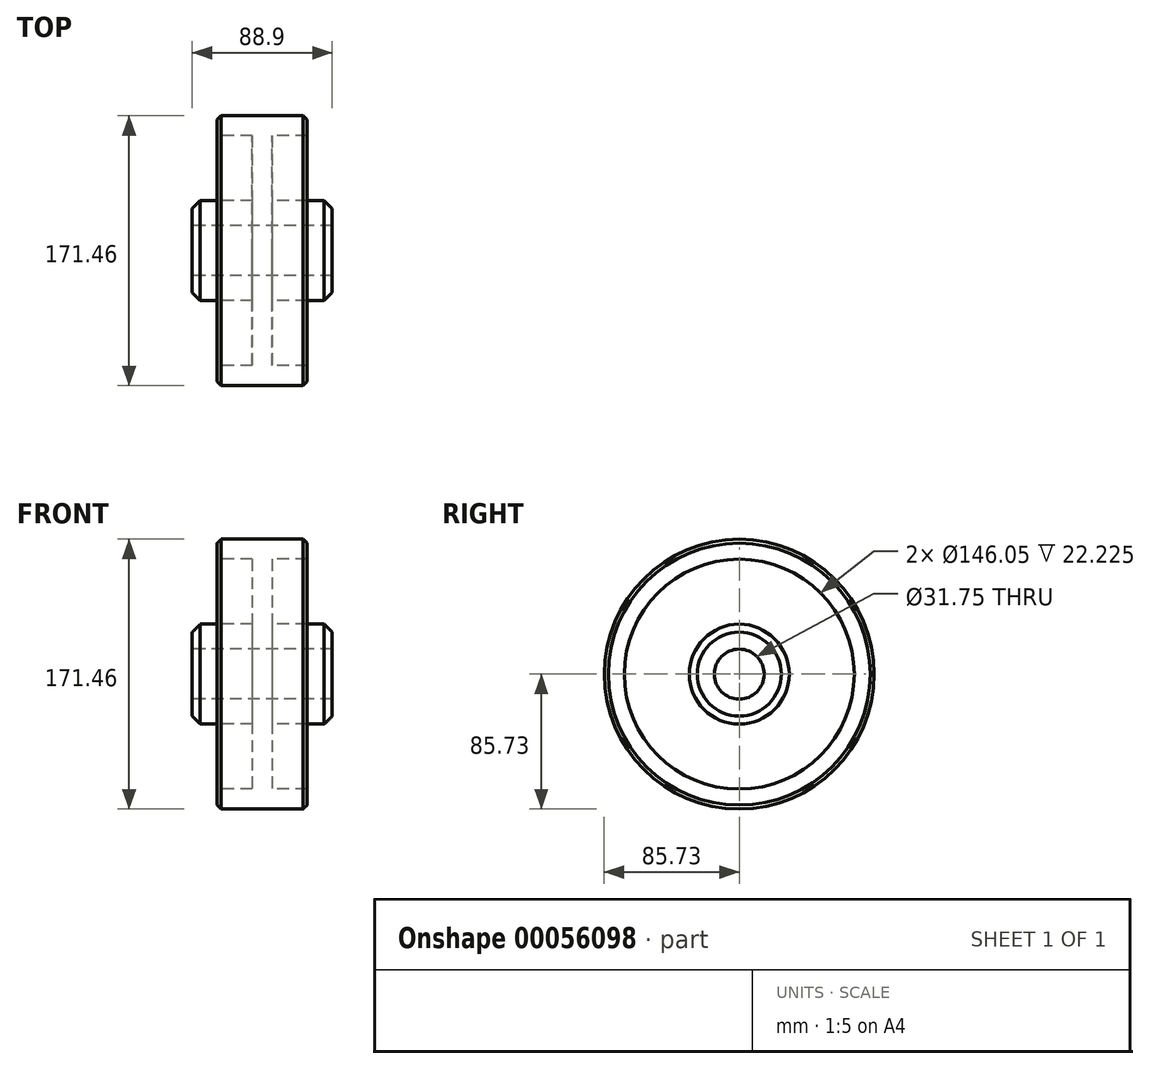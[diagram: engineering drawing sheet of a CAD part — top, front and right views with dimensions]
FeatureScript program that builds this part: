
annotation { "Feature Type Name" : "Feature", "Feature Type Description" : "" }
export const myFeature = defineFeature(function(context is Context, id is Id, definition is map)
    precondition{}
    {
        {
            var Q0;
            Q0=qCreatedBy(makeId("Front.planeOp"),FACE);
            var sketch = newSketch(context, id + "F0", { "sketchPlane" : qUnion([Q0])});
            skLineSegment(sketch, "E0", {"start": v(-28.57, 85.73) * mm, "end": v(28.57, 85.73) * mm});
            skLineSegment(sketch, "E1", {"start": v(28.57, 85.73) * mm, "end": v(28.57, 73.03) * mm});
            skLineSegment(sketch, "E2", {"start": v(28.57, 73.02) * mm, "end": v(6.35, 73.02) * mm});
            skLineSegment(sketch, "E3", {"start": v(6.35, 73.02) * mm, "end": v(6.35, 31.75) * mm});
            skLineSegment(sketch, "E4", {"start": v(6.35, 31.75) * mm, "end": v(44.45, 31.75) * mm});
            skLineSegment(sketch, "E5", {"start": v(44.45, 31.75) * mm, "end": v(44.45, 15.88) * mm});
            skLineSegment(sketch, "E6", {"start": v(44.45, 15.88) * mm, "end": v(-44.45, 15.87) * mm});
            skLineSegment(sketch, "E7", {"start": v(-44.45, 15.88) * mm, "end": v(-44.45, 31.75) * mm});
            skLineSegment(sketch, "E8", {"start": v(-44.45, 31.75) * mm, "end": v(-6.35, 31.75) * mm});
            skLineSegment(sketch, "E9", {"start": v(-6.35, 31.75) * mm, "end": v(-6.35, 73.02) * mm});
            skLineSegment(sketch, "E10", {"start": v(-6.35, 73.02) * mm, "end": v(-28.57, 73.02) * mm});
            skLineSegment(sketch, "E11", {"start": v(-28.58, 73.03) * mm, "end": v(-28.58, 85.73) * mm});
            skLineSegment(sketch, "E12", {"start": v(0, 0) * mm, "end": v(0, 277.02) * mm, "construction": true});
            skLineSegment(sketch, "E13", {"start": v(-347.66, 0) * mm, "end": v(344.49, 0) * mm, "construction": true});
            skSolve(sketch);
        }
        {
            var Q0;
            Q0 = qSketchRegion(id + "F0", true);
            var Q1;
            Q1=sQuery(id+"F0.wireOp",EDGE,"E13");
            revolve(context, id + "F1", {"entities" : qUnion([Q0]), "axis" : qUnion([Q1]), "revolveType" : RevolveType.FULL});
        }
        {
            var Q0;
            Q0=makeQuery(id+"F1.opRevolve","SWEPT_EDGE",EDGE,{"disambiguationData":[OSD([sQuery(id+"F0.wireOp",EDGE,"E0"),sQuery(id+"F0.wireOp",EDGE,"E11")])]});
            var Q1;
            Q1=makeQuery(id+"F1.opRevolve","SWEPT_EDGE",EDGE,{"disambiguationData":[OSD([sQuery(id+"F0.wireOp",EDGE,"E0"),sQuery(id+"F0.wireOp",EDGE,"E1")])]});
            chamfer(context, id + "F2", {"entities" : qUnion([Q0, Q1]), "width" : 2.54 * mm, "tangentPropagation" : true});
        }
        {
            var Q0;
            Q0=makeQuery(id+"F1.opRevolve","SWEPT_EDGE",EDGE,{"disambiguationData":[OSD([sQuery(id+"F0.wireOp",EDGE,"E4"),sQuery(id+"F0.wireOp",EDGE,"E5")])]});
            var Q1;
            Q1=makeQuery(id+"F1.opRevolve","SWEPT_EDGE",EDGE,{"disambiguationData":[OSD([sQuery(id+"F0.wireOp",EDGE,"E7"),sQuery(id+"F0.wireOp",EDGE,"E8")])]});
            chamfer(context, id + "F3", {"entities" : qUnion([Q0, Q1]), "width" : 5.08 * mm, "tangentPropagation" : true});
        }
    });
